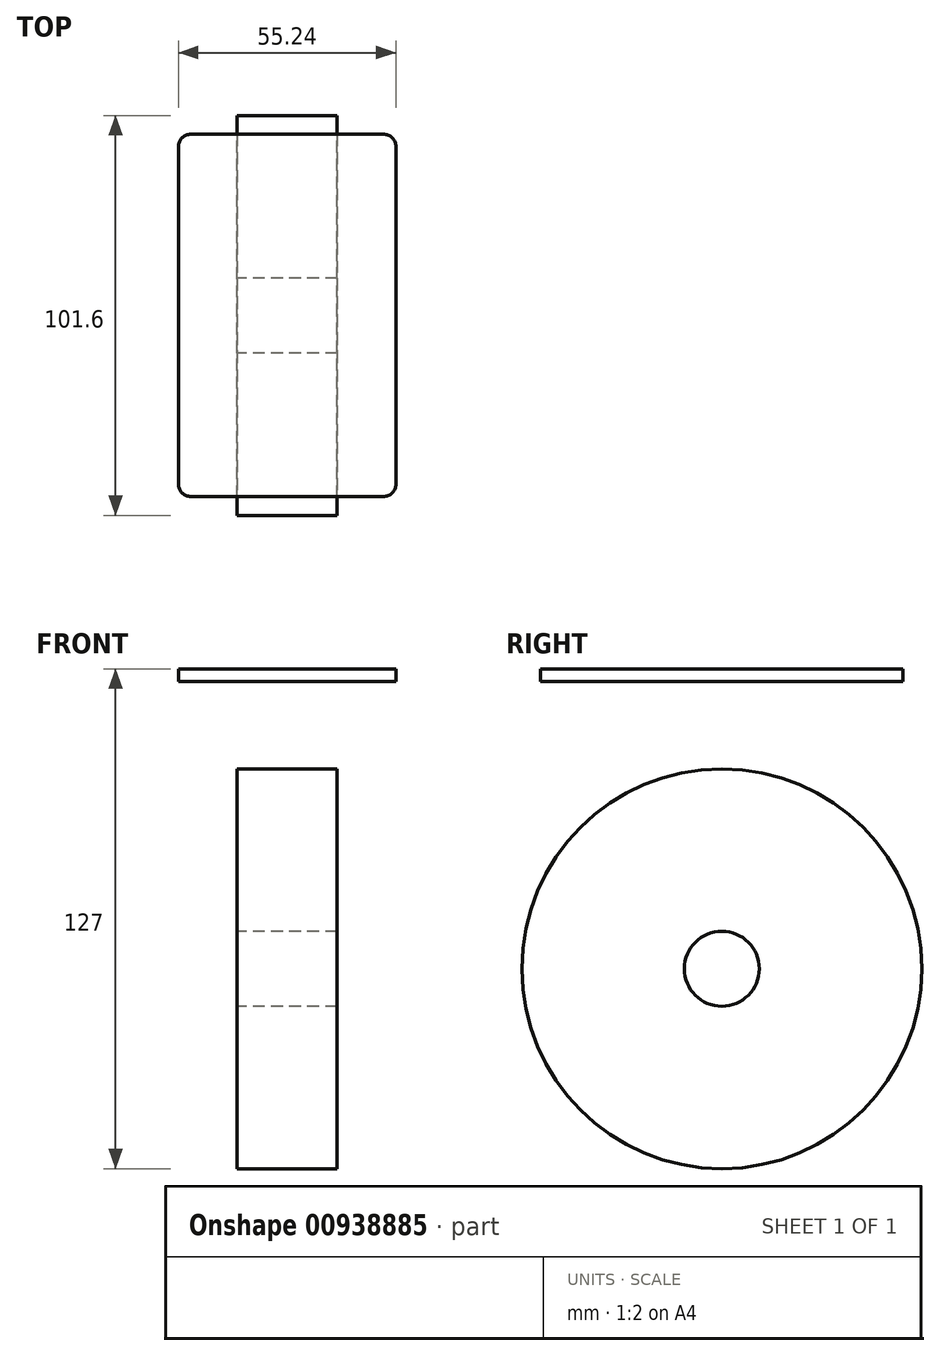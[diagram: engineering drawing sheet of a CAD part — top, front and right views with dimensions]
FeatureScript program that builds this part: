
annotation { "Feature Type Name" : "Feature", "Feature Type Description" : "" }
export const myFeature = defineFeature(function(context is Context, id is Id, definition is map)
    precondition{}
    {
        {
            var Q0;
            Q0=qCreatedBy(makeId("Right.planeOp"),FACE);
            var sketch = newSketch(context, id + "F0", { "sketchPlane" : qUnion([Q0])});
            skCircle(sketch, "E0", {"center": v(0, 0) * mm, "radius": 50.8 * mm});
            skCircle(sketch, "E1", {"center": v(0, 0) * mm, "radius": 9.53 * mm});
            skSolve(sketch);
        }
        {
            var Q0;
            Q0=makeQuery(id+"F0.imprint","IMPRINT",FACE,{"disambiguationData":[TD([[makeQuery(id+"F0.imprint","IMPRINT",EDGE,{"derivedFrom":sQuery(id+"F0.wireOp",EDGE,"E0")}),1.0]])]});
            extrude(context, id + "F1", {"entities" : qUnion([Q0]), "endBound" : BoundingType.SYMMETRIC, "depth" : 25.4 * mm, "offsetDistance" : 25.4 * mm});
        }
        {
            var Q0;
            Q0=qCreatedBy(makeId("Top.planeOp"),FACE);
            cPlane(context, id + "F2", {"entities" : qUnion([Q0]), "cplaneType" : CPlaneType.OFFSET, "offset" : 76.2 * mm, "width" : 152.4 * mm, "height" : 152.4 * mm});
        }
        {
            var Q0;
            Q0=qCreatedBy(id+"F2.planeOp",FACE);
            var sketch = newSketch(context, id + "F3", { "sketchPlane" : qUnion([Q0])});
            skLineSegment(sketch, "E2.bottom", {"start": v(24.45, 46.04) * mm, "end": v(-24.45, 46.04) * mm});
            skLineSegment(sketch, "E2.top", {"start": v(24.45, -46.04) * mm, "end": v(-24.45, -46.04) * mm});
            skLineSegment(sketch, "E2.left", {"start": v(27.62, 42.86) * mm, "end": v(27.62, -42.86) * mm});
            skLineSegment(sketch, "E2.right", {"start": v(-27.62, 42.86) * mm, "end": v(-27.62, -42.86) * mm});
            skPoint(sketch, "E2.middle", {"position": v(0, 0) * mm});
            skPoint(sketch, "E3.visualSharp", {"position": v(-27.62, 46.04) * mm});
            skArc(sketch, "E3.filletArc", {"start": v(-24.45, 46.04) * mm, "mid": v(-26.7, 45.1) * mm, "end": v(-27.62, 42.86) * mm});
            skPoint(sketch, "E4.visualSharp", {"position": v(27.62, 46.04) * mm});
            skArc(sketch, "E4.filletArc", {"start": v(27.62, 42.86) * mm, "mid": v(26.7, 45.1) * mm, "end": v(24.45, 46.04) * mm});
            skPoint(sketch, "E5.visualSharp", {"position": v(27.62, -46.04) * mm});
            skArc(sketch, "E5.filletArc", {"start": v(24.45, -46.04) * mm, "mid": v(26.7, -45.1) * mm, "end": v(27.62, -42.86) * mm});
            skPoint(sketch, "E6.visualSharp", {"position": v(-27.62, -46.04) * mm});
            skArc(sketch, "E6.filletArc", {"start": v(-27.62, -42.86) * mm, "mid": v(-26.7, -45.1) * mm, "end": v(-24.45, -46.04) * mm});
            skSolve(sketch);
        }
        {
            var Q0;
            Q0 = qSketchRegion(id + "F3", true);
            extrude(context, id + "F4", {"entities" : qUnion([Q0]), "oppositeDirection" : true, "depth" : 3.17 * mm, "offsetDistance" : 25.4 * mm});
        }
    });
